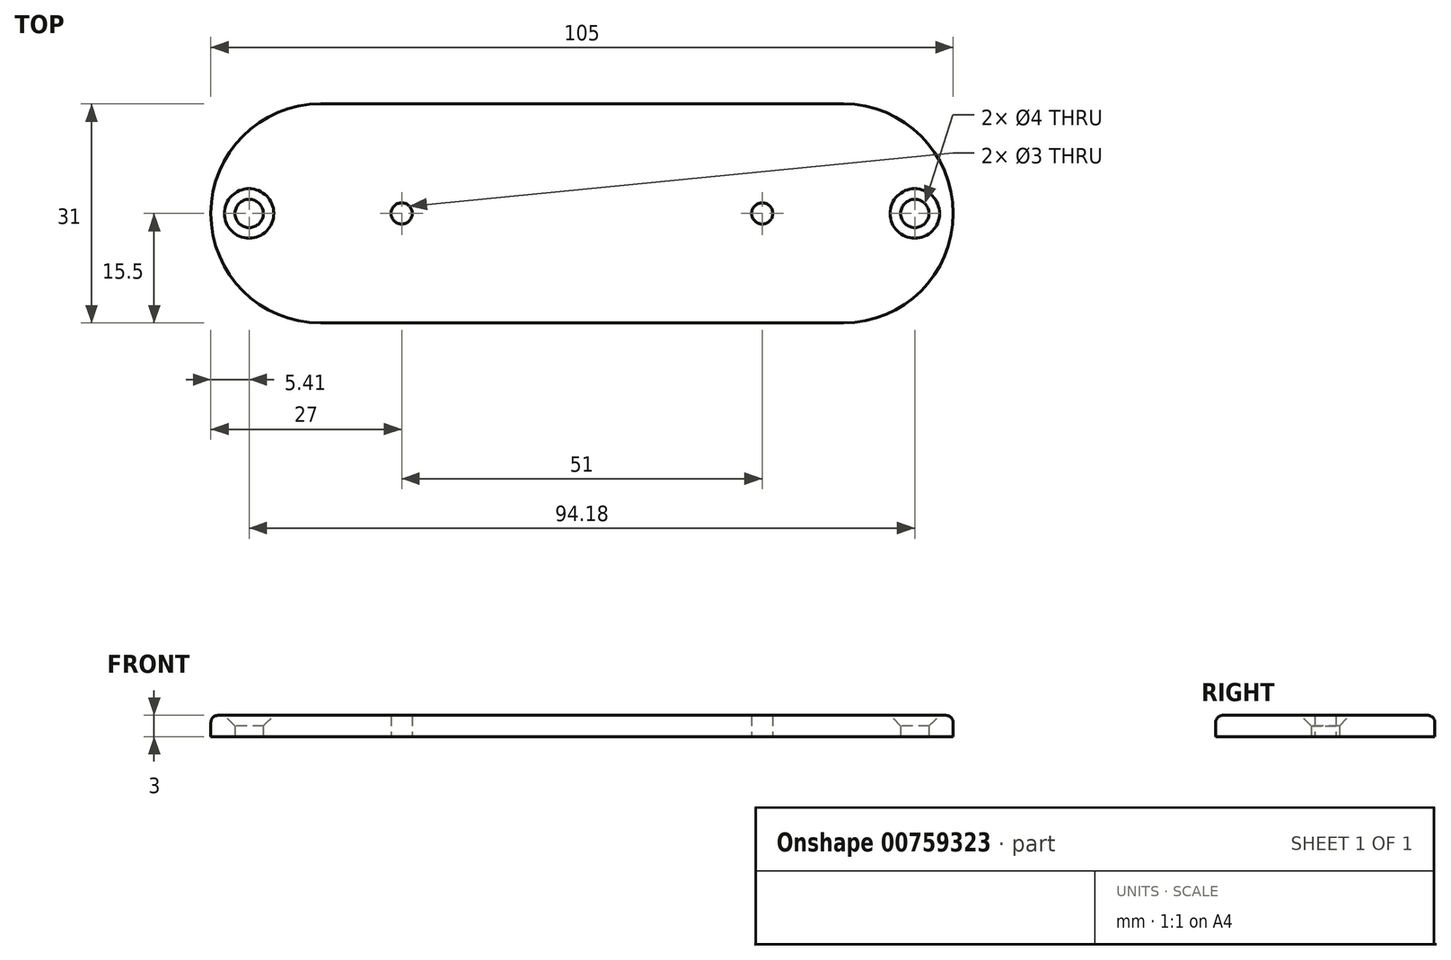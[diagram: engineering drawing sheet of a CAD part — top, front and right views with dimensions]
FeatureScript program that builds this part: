
annotation { "Feature Type Name" : "Feature", "Feature Type Description" : "" }
export const myFeature = defineFeature(function(context is Context, id is Id, definition is map)
    precondition{}
    {
        {
            var Q0;
            Q0=qCreatedBy(makeId("Top.planeOp"),FACE);
            var sketch = newSketch(context, id + "F0", { "sketchPlane" : qUnion([Q0])});
            skLineSegment(sketch, "E0.bottom", {"start": v(-37, 15.5) * mm, "end": v(37, 15.5) * mm});
            skLineSegment(sketch, "E0.top", {"start": v(-37, -15.5) * mm, "end": v(37, -15.5) * mm});
            skPoint(sketch, "E0.middle", {"position": v(0, 0) * mm});
            skCircle(sketch, "E1", {"center": v(47.09, 0) * mm, "radius": 2 * mm});
            skCircle(sketch, "E2", {"center": v(25.5, 0) * mm, "radius": 1.5 * mm});
            skCircle(sketch, "E3", {"center": v(-25.5, 0) * mm, "radius": 1.5 * mm});
            skCircle(sketch, "E4", {"center": v(-47.1, 0) * mm, "radius": 2 * mm});
            skArc(sketch, "E5", {"start": v(-37, 15.5) * mm, "mid": v(-52.5, 0) * mm, "end": v(-37, -15.5) * mm});
            skArc(sketch, "E6", {"start": v(37, 15.5) * mm, "mid": v(52.5, 0) * mm, "end": v(37, -15.5) * mm});
            skLineSegment(sketch, "E7", {"start": v(-52.5, 0) * mm, "end": v(-52.5, 5.2) * mm, "construction": true});
            skLineSegment(sketch, "E8", {"start": v(-52.5, 5.2) * mm, "end": v(-51.6, 5.2) * mm, "construction": true});
            skLineSegment(sketch, "E9", {"start": v(52.5, 5.2) * mm, "end": v(52.5, 0) * mm, "construction": true});
            skLineSegment(sketch, "E10.trimOffspring", {"start": v(51.6, 5.2) * mm, "end": v(52.5, 5.2) * mm, "construction": true});
            skSolve(sketch);
        }
        {
            var Q0;
            Q0=makeQuery(id+"F0.imprint","IMPRINT",FACE,{"disambiguationData":[TD([[makeQuery(id+"F0.imprint","IMPRINT",EDGE,{"derivedFrom":sQuery(id+"F0.wireOp",EDGE,"E0.bottom")}),-1.0]])]});
            extrude(context, id + "F1", {"entities" : qUnion([Q0]), "depth" : 3 * mm, "offsetDistance" : 25 * mm});
        }
        {
            var Q0;
            Q0=makeQuery(id+"F1.opExtrude","CAP_EDGE",EDGE,{"disambiguationData":[OSD([sQuery(id+"F0.wireOp",EDGE,"E5")])],"isStart":false});
            fillet(context, id + "F2", {"entities" : qUnion([Q0]), "radius" : 1 * mm, "tangentPropagation" : true, "allowEdgeOverflow" : false});
        }
        {
            var Q0;
            Q0=makeQuery(id+"F1.opExtrude","CAP_EDGE",EDGE,{"disambiguationData":[OSD([sQuery(id+"F0.wireOp",EDGE,"E4")])],"isStart":false});
            var Q1;
            Q1=makeQuery(id+"F1.opExtrude","CAP_EDGE",EDGE,{"disambiguationData":[OSD([sQuery(id+"F0.wireOp",EDGE,"E1")])],"isStart":false});
            chamfer(context, id + "F3", {"entities" : qUnion([Q0, Q1]), "width" : 1.5 * mm, "tangentPropagation" : true});
        }
    });
